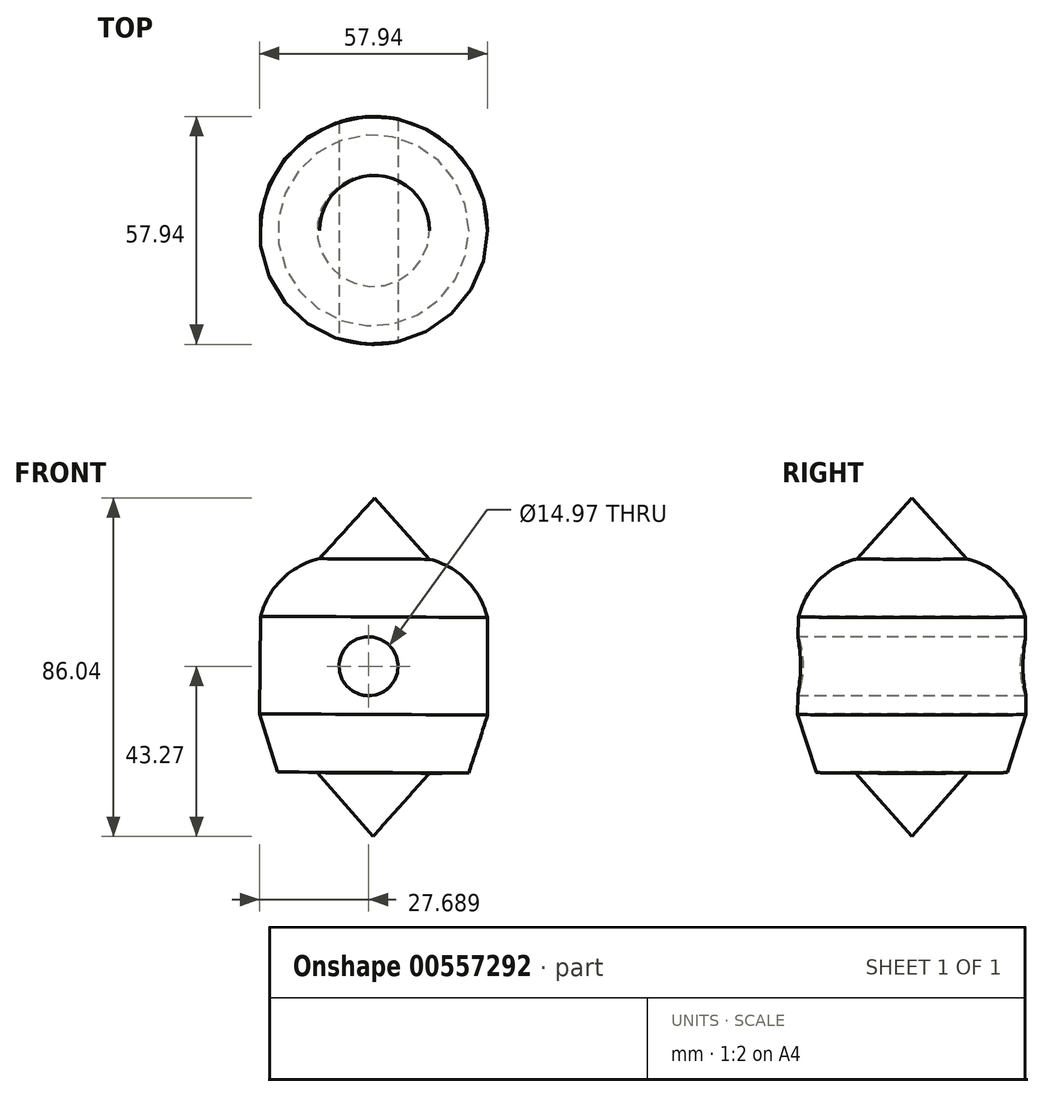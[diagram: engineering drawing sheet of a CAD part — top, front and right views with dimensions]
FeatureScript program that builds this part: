
annotation { "Feature Type Name" : "Feature", "Feature Type Description" : "" }
export const myFeature = defineFeature(function(context is Context, id is Id, definition is map)
    precondition{}
    {
        {
            var Q0;
            Q0=qCreatedBy(makeId("Front.planeOp"),FACE);
            var sketch = newSketch(context, id + "F0", { "sketchPlane" : qUnion([Q0])});
            skLineSegment(sketch, "E0", {"start": v(-23.9, 42.77) * mm, "end": v(-24.35, -43.27) * mm});
            skLineSegment(sketch, "E1", {"start": v(-23.9, 42.77) * mm, "end": v(-10, 27.18) * mm});
            skLineSegment(sketch, "E2", {"start": v(-10, 27.18) * mm, "end": v(0, 27.13) * mm});
            skLineSegment(sketch, "E3", {"start": v(0, 27.13) * mm, "end": v(4.78, 12.4) * mm});
            skLineSegment(sketch, "E4", {"start": v(4.78, 12.4) * mm, "end": v(4.78, 0) * mm});
            skPoint(sketch, "E5.startSnap0", {"position": v(-24.13, -0.25) * mm});
            skLineSegment(sketch, "E6.MirrorCS", {"start": v(4.78, -12.4) * mm, "end": v(4.78, 0) * mm});
            skLineSegment(sketch, "E7.MirrorCS", {"start": v(0, -27.13) * mm, "end": v(4.78, -12.4) * mm});
            skLineSegment(sketch, "E8.MirrorCS", {"start": v(-10, -27.18) * mm, "end": v(0, -27.13) * mm});
            skLineSegment(sketch, "E9.MirrorCS", {"start": v(-24.35, -43.27) * mm, "end": v(-10, -27.18) * mm});
            skSolve(sketch);
        }
        {
            var Q0;
            Q0=makeQuery(id+"F0.imprint","IMPRINT",FACE,{"disambiguationData":[TD([[makeQuery(id+"F0.imprint","IMPRINT",EDGE,{"derivedFrom":sQuery(id+"F0.wireOp",EDGE,"E0")}),1.0]])]});
            var Q1;
            Q1=sQuery(id+"F0.wireOp",EDGE,"E0");
            revolve(context, id + "F1", {"entities" : qUnion([Q0]), "axis" : qUnion([Q1]), "revolveType" : RevolveType.FULL});
        }
        {
            var Q0;
            Q0=qCreatedBy(makeId("Front.planeOp"),FACE);
            var sketch = newSketch(context, id + "F2", { "sketchPlane" : qUnion([Q0])});
            skCircle(sketch, "E10", {"center": v(-25.47, 0) * mm, "radius": 7.49 * mm});
            skSolve(sketch);
        }
        {
            var Q0;
            Q0 = qSketchRegion(id + "F2", true);
            extrude(context, id + "F3", {"entities" : qUnion([Q0]), "operationType" : NewBodyOperationType.REMOVE, "oppositeDirection" : true, "depth" : 38.4 * mm, "offsetDistance" : 25 * mm, "hasSecondDirection" : true, "secondDirectionBound" : SecondDirectionBoundingType.THROUGH_ALL, "secondDirectionOppositeDirection" : false, "secondDirectionDepth" : 25 * mm});
        }
        {
            var Q0;
            Q0=makeQuery(id+"F1.opRevolve","SWEPT_EDGE",EDGE,{"disambiguationData":[OSD([sQuery(id+"F0.wireOp",EDGE,"E2"),sQuery(id+"F0.wireOp",EDGE,"E3")])]});
            fillet(context, id + "F4", {"entities" : qUnion([Q0]), "radius" : 20 * mm, "tangentPropagation" : true, "allowEdgeOverflow" : false});
        }
    });
